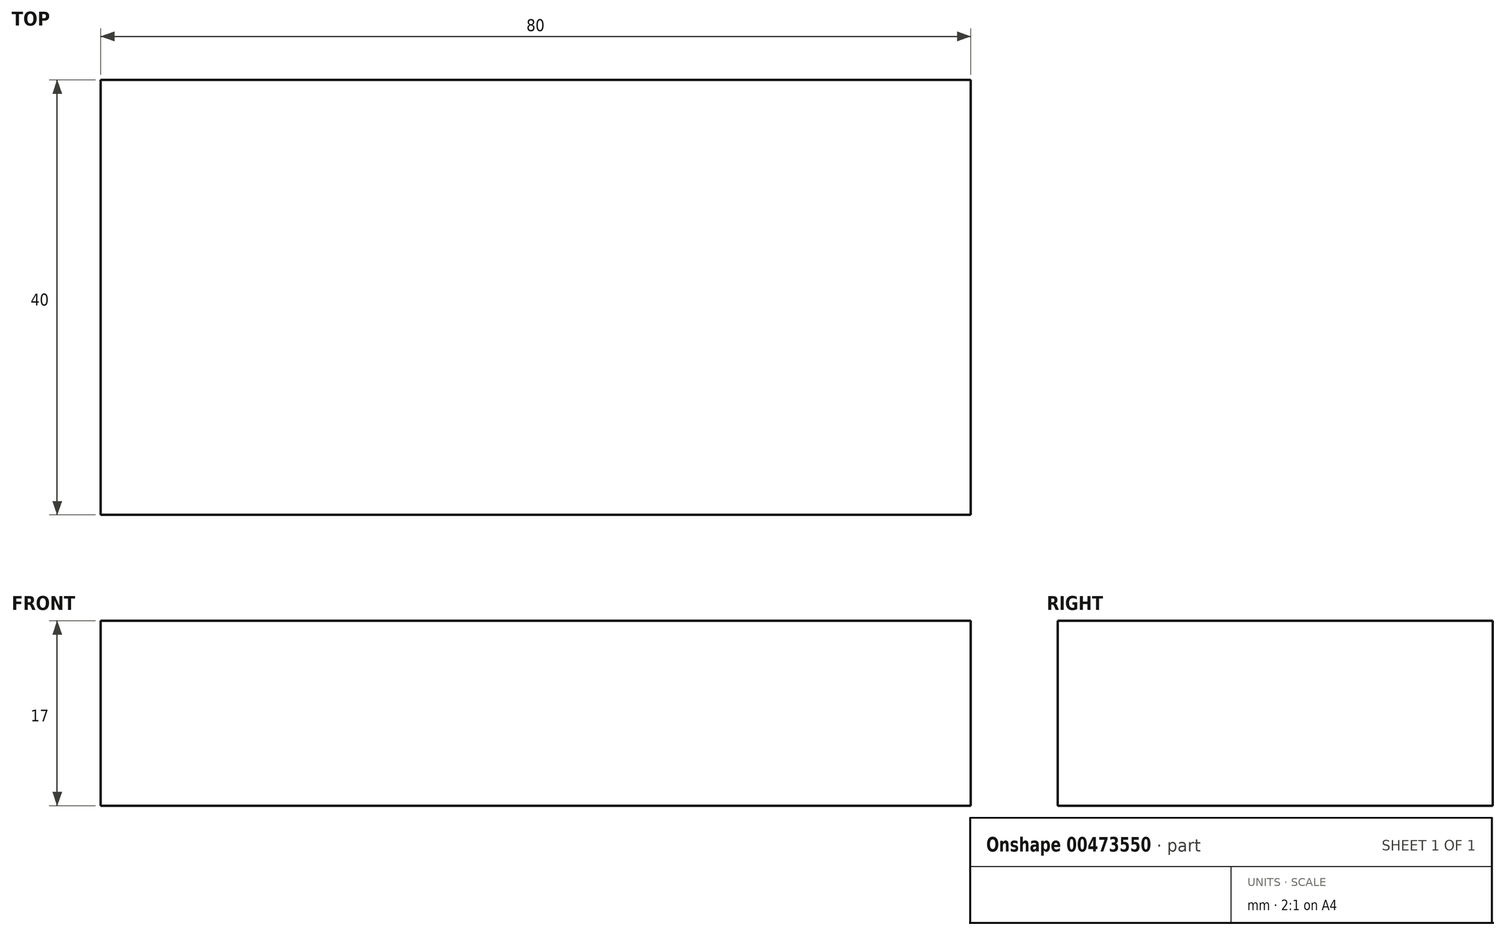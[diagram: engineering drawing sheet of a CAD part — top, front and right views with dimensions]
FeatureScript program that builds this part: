
annotation { "Feature Type Name" : "Feature", "Feature Type Description" : "" }
export const myFeature = defineFeature(function(context is Context, id is Id, definition is map)
    precondition{}
    {
        {
            var Q0;
            Q0=qCreatedBy(makeId("Top.planeOp"),FACE);
            var sketch = newSketch(context, id + "F0", { "sketchPlane" : qUnion([Q0])});
            skLineSegment(sketch, "E0.bottom", {"start": v(-38.34, 21.22) * mm, "end": v(41.66, 21.22) * mm});
            skLineSegment(sketch, "E0.top", {"start": v(-38.34, -18.78) * mm, "end": v(41.66, -18.78) * mm});
            skLineSegment(sketch, "E0.left", {"start": v(-38.34, 21.22) * mm, "end": v(-38.34, -18.78) * mm});
            skLineSegment(sketch, "E0.right", {"start": v(41.66, 21.22) * mm, "end": v(41.66, -18.78) * mm});
            skSolve(sketch);
        }
        {
            var Q0;
            Q0 = qSketchRegion(id + "F0", true);
            extrude(context, id + "F1", {"entities" : qUnion([Q0]), "depth" : 17 * mm});
        }
    });
